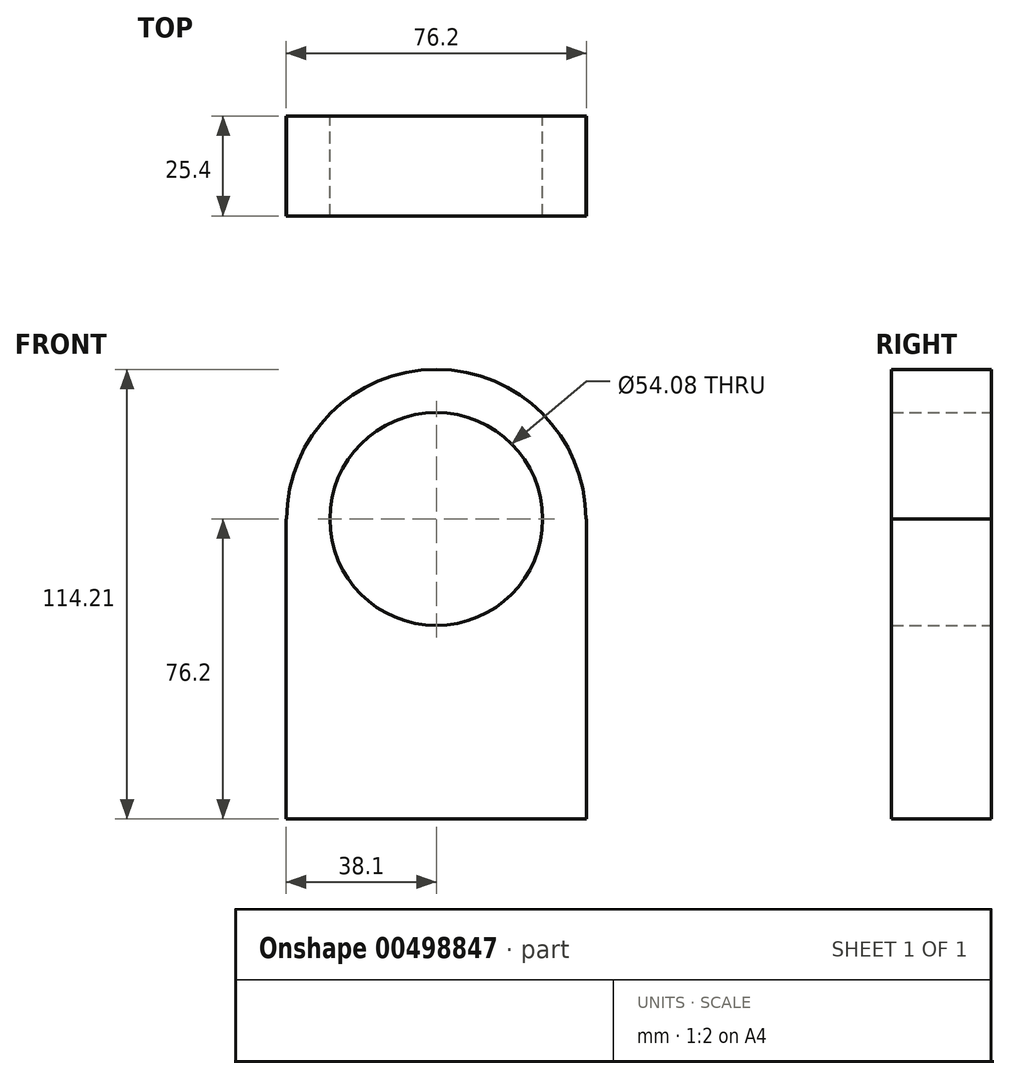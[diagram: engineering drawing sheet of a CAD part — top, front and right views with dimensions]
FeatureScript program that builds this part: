
annotation { "Feature Type Name" : "Feature", "Feature Type Description" : "" }
export const myFeature = defineFeature(function(context is Context, id is Id, definition is map)
    precondition{}
    {
        {
            var Q0;
            Q0=qCreatedBy(makeId("Front.planeOp"),FACE);
            var sketch = newSketch(context, id + "F0", { "sketchPlane" : qUnion([Q0])});
            skLineSegment(sketch, "E0.bottom", {"start": v(38.1, -38.1) * mm, "end": v(-38.1, -38.1) * mm});
            skLineSegment(sketch, "E0.top", {"start": v(38.1, 38.1) * mm, "end": v(38, 38.1) * mm});
            skLineSegment(sketch, "E0.left", {"start": v(38.1, -38.1) * mm, "end": v(38.1, 38.1) * mm});
            skLineSegment(sketch, "E0.right", {"start": v(-38.1, -38.1) * mm, "end": v(-38.1, 38.1) * mm});
            skPoint(sketch, "E0.middle", {"position": v(0, 0) * mm});
            skArc(sketch, "E1", {"start": v(38, 38.1) * mm, "mid": v(0, 76.1) * mm, "end": v(-38, 38.1) * mm});
            skCircle(sketch, "E2", {"center": v(0, 38.1) * mm, "radius": 27.04 * mm});
            skLineSegment(sketch, "E3.trimOffspring", {"start": v(-38, 38.1) * mm, "end": v(-38.1, 38.1) * mm});
            skSolve(sketch);
        }
        {
            var Q0;
            Q0=makeQuery(id+"F0.imprint","IMPRINT",FACE,{"disambiguationData":[TD([[makeQuery(id+"F0.imprint","IMPRINT",EDGE,{"derivedFrom":sQuery(id+"F0.wireOp",EDGE,"E0.bottom")}),-1.0]])]});
            extrude(context, id + "F1", {"entities" : qUnion([Q0]), "depth" : 25.4 * mm, "offsetDistance" : 25.4 * mm});
        }
    });
